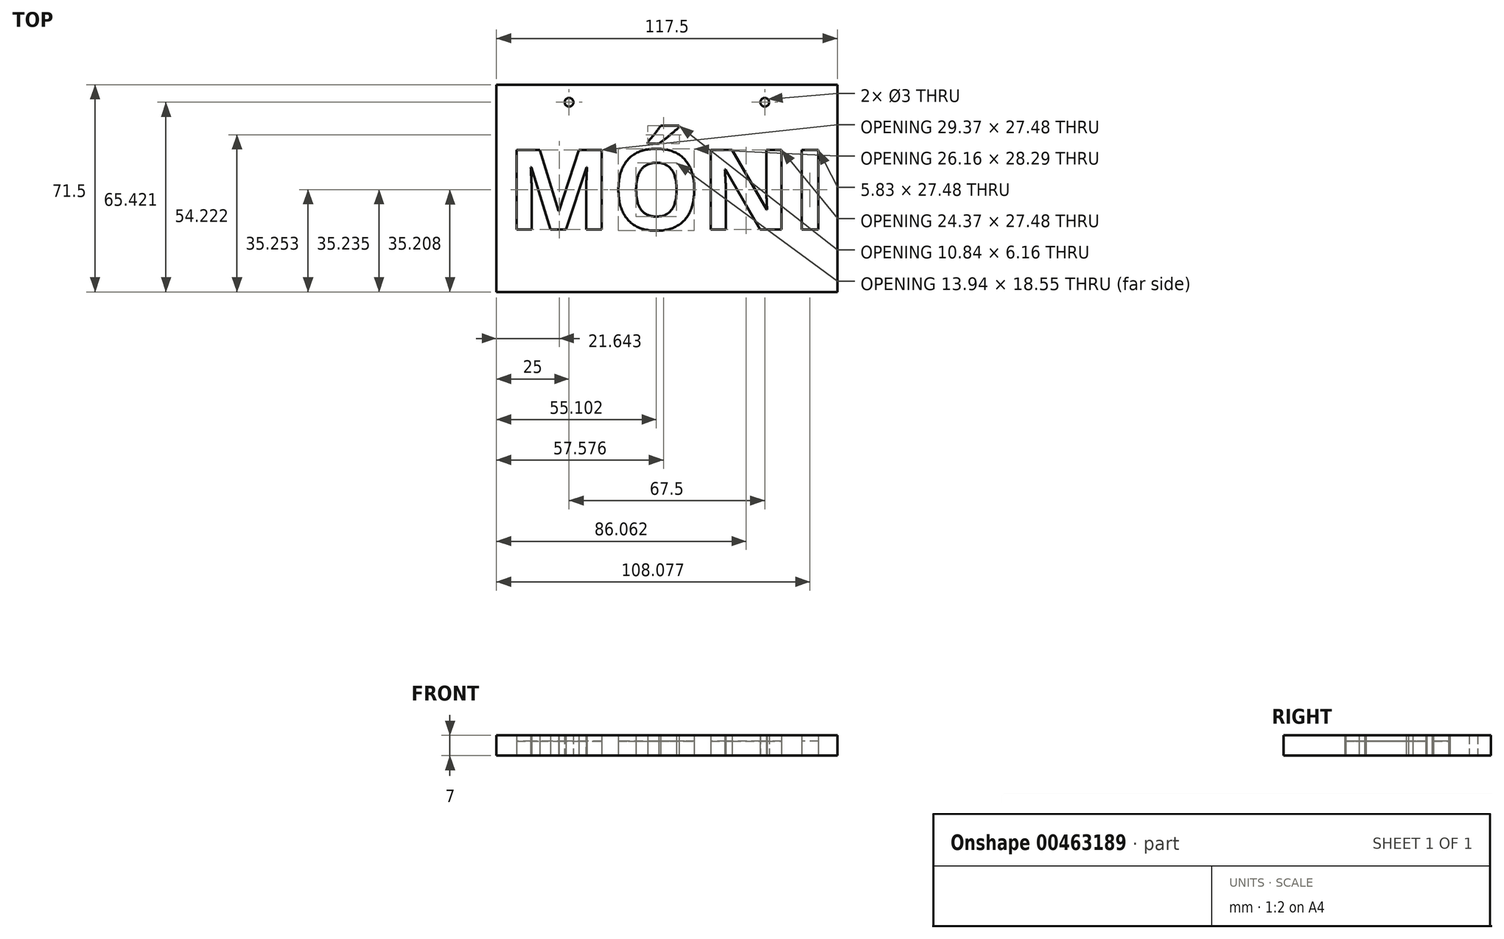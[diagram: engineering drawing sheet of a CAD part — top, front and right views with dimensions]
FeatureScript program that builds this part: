
annotation { "Feature Type Name" : "Feature", "Feature Type Description" : "" }
export const myFeature = defineFeature(function(context is Context, id is Id, definition is map)
    precondition{}
    {
        {
            var Q0;
            Q0=qCreatedBy(makeId("Top.planeOp"),FACE);
            var sketch = newSketch(context, id + "F0", { "sketchPlane" : qUnion([Q0])});
            skLineSegment(sketch, "E0.bottom", {"start": v(58.75, -35.75) * mm, "end": v(-58.75, -35.75) * mm});
            skLineSegment(sketch, "E0.top", {"start": v(58.75, 35.75) * mm, "end": v(-58.75, 35.75) * mm});
            skLineSegment(sketch, "E0.left", {"start": v(58.75, -35.75) * mm, "end": v(58.75, 35.75) * mm});
            skLineSegment(sketch, "E0.right", {"start": v(-58.75, -35.75) * mm, "end": v(-58.75, 35.75) * mm});
            skPoint(sketch, "E0.middle", {"position": v(0, 0) * mm});
            skCircle(sketch, "E1", {"center": v(-33.75, 29.67) * mm, "radius": 1.5 * mm});
            skCircle(sketch, "E2", {"center": v(33.75, 29.67) * mm, "radius": 1.5 * mm});
            skText(sketch, "E3", { "text": "MÓNI", "fontName": "OpenSans-Bold.ttf"});
            const initialGuessF0  = {"E3": [-0.05525, -0.01428, 1, 0, 0.02771]};
            skSetInitialGuess(sketch, initialGuessF0);
            skSolve(sketch);
        }
        {
            var Q0;
            Q0=makeQuery(id+"F0.imprint","IMPRINT",FACE,{"disambiguationData":[TD([[makeQuery(id+"F0.imprint","IMPRINT",EDGE,{"derivedFrom":sQuery(id+"F0.wireOp",EDGE,"E0.bottom")}),-1.0]])]});
            var Q1;
            Q1=makeQuery(id+"F0.imprint","IMPRINT",FACE,{"disambiguationData":[TD([[makeQuery(id+"F0.imprint","IMPRINT",EDGE,{"derivedFrom":sQuery(id+"F0.wireOp",EDGE,"E3.sketch_text.stroke-27")}),1.0]])]});
            extrude(context, id + "F1", {"entities" : qUnion([Q0, Q1]), "depth" : 7 * mm});
        }
        {
            var Q0;
            Q0=makeQuery(id+"F0.imprint","IMPRINT",FACE,{"disambiguationData":[TD([[makeQuery(id+"F0.imprint","IMPRINT",EDGE,{"derivedFrom":sQuery(id+"F0.wireOp",EDGE,"E3.sketch_text.stroke-0")}),-1.0]])]});
            var Q1;
            Q1=makeQuery(id+"F0.imprint","IMPRINT",FACE,{"disambiguationData":[TD([[makeQuery(id+"F0.imprint","IMPRINT",EDGE,{"derivedFrom":sQuery(id+"F0.wireOp",EDGE,"E3.sketch_text.stroke-19")}),-1.0]])]});
            var Q2;
            Q2=makeQuery(id+"F0.imprint","IMPRINT",FACE,{"disambiguationData":[TD([[makeQuery(id+"F0.imprint","IMPRINT",EDGE,{"derivedFrom":sQuery(id+"F0.wireOp",EDGE,"E3.sketch_text.stroke-40")}),-1.0]])]});
            var Q3;
            Q3=makeQuery(id+"F0.imprint","IMPRINT",FACE,{"disambiguationData":[TD([[makeQuery(id+"F0.imprint","IMPRINT",EDGE,{"derivedFrom":sQuery(id+"F0.wireOp",EDGE,"E3.sketch_text.stroke-54")}),-1.0]])]});
            var Q4;
            Q4=makeQuery(id+"F0.imprint","IMPRINT",FACE,{"disambiguationData":[TD([[makeQuery(id+"F0.imprint","IMPRINT",EDGE,{"derivedFrom":sQuery(id+"F0.wireOp",EDGE,"E3.sketch_text.stroke-33")}),-1.0]])]});
            extrude(context, id + "F2", {"entities" : qUnion([Q0, Q1, Q2, Q3, Q4]), "depth" : 5 * mm});
        }
    });
